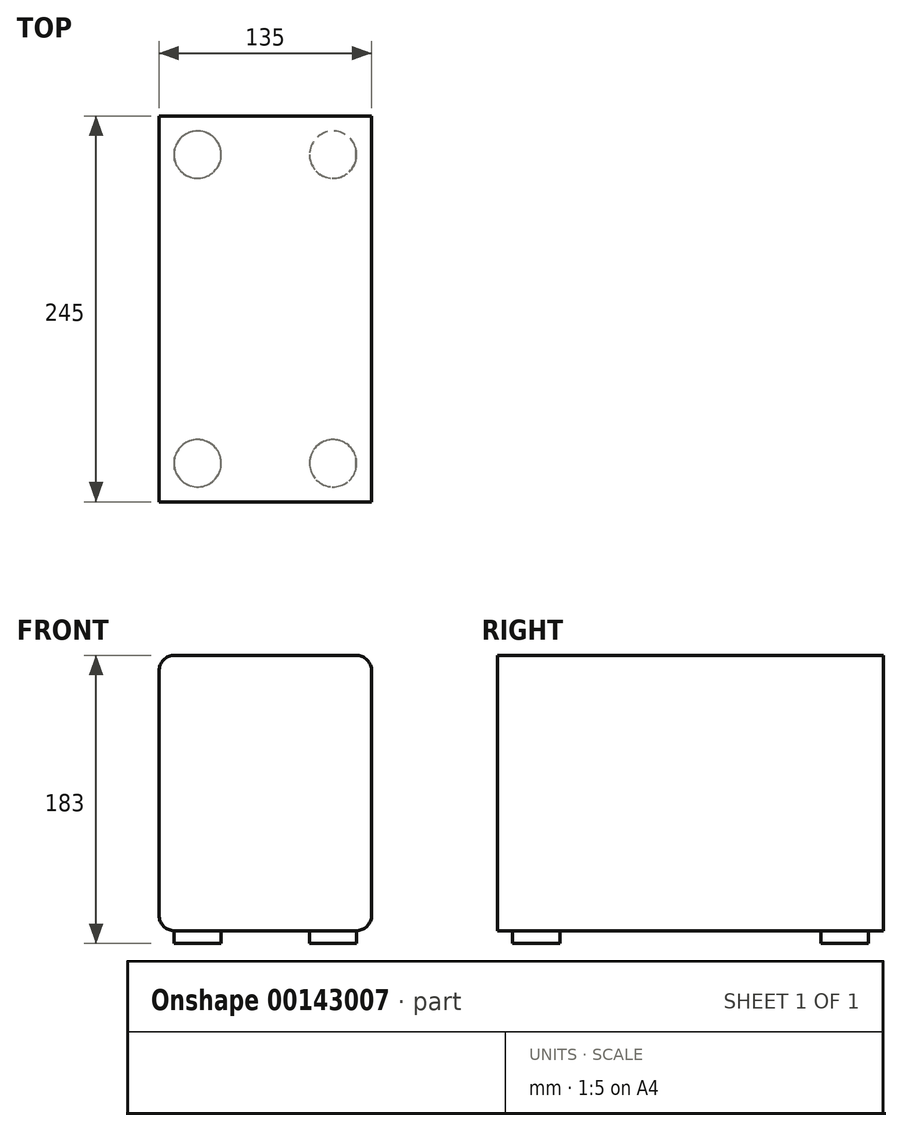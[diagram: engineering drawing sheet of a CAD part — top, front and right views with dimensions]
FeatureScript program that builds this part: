
annotation { "Feature Type Name" : "Feature", "Feature Type Description" : "" }
export const myFeature = defineFeature(function(context is Context, id is Id, definition is map)
    precondition{}
    {
        {
            var Q0;
            Q0=qCreatedBy(makeId("Front.planeOp"),FACE);
            var sketch = newSketch(context, id + "F0", { "sketchPlane" : qUnion([Q0])});
            skLineSegment(sketch, "E0.bottom", {"start": v(10, 0) * mm, "end": v(125, 0) * mm});
            skLineSegment(sketch, "E0.top", {"start": v(10, 175) * mm, "end": v(125, 175) * mm});
            skLineSegment(sketch, "E0.left", {"start": v(0, 10) * mm, "end": v(0, 165) * mm});
            skLineSegment(sketch, "E0.right", {"start": v(135, 10) * mm, "end": v(135, 165) * mm});
            skPoint(sketch, "E1.visualSharp", {"position": v(135, 175) * mm});
            skArc(sketch, "E1.filletArc", {"start": v(135, 165) * mm, "mid": v(132.07, 172.07) * mm, "end": v(125, 175) * mm});
            skPoint(sketch, "E2.visualSharp", {"position": v(0, 175) * mm});
            skArc(sketch, "E2.filletArc", {"start": v(10, 175) * mm, "mid": v(2.93, 172.07) * mm, "end": v(0, 165) * mm});
            skPoint(sketch, "E3.visualSharp", {"position": v(135, 0) * mm});
            skArc(sketch, "E3.filletArc", {"start": v(125, 0) * mm, "mid": v(132.07, 2.93) * mm, "end": v(135, 10) * mm});
            skPoint(sketch, "E4.visualSharp", {"position": v(0, 0) * mm});
            skArc(sketch, "E4.filletArc", {"start": v(0, 10) * mm, "mid": v(2.93, 2.93) * mm, "end": v(10, 0) * mm});
            skSolve(sketch);
        }
        {
            var Q0;
            Q0 = qSketchRegion(id + "F0", true);
            extrude(context, id + "F1", {"entities" : qUnion([Q0]), "depth" : 245 * mm});
        }
        {
            var Q0;
            Q0=makeQuery(id+"F1.opExtrude","SWEPT_FACE",FACE,{"disambiguationData":[OSD([sQuery(id+"F0.wireOp",EDGE,"E0.bottom")])]});
            var sketch = newSketch(context, id + "F2", { "sketchPlane" : qUnion([Q0])});
            skPoint(sketch, "E5", {"position": v(24.48, 220.52) * mm});
            skCircle(sketch, "E6", {"center": v(24.48, 220.52) * mm, "radius": 15 * mm});
            skLineSegment(sketch, "E7", {"start": v(67.5, 253.64) * mm, "end": v(67.5, 0) * mm, "construction": true});
            skPoint(sketch, "E7.startSnap0", {"position": v(67.5, 245) * mm});
            skCircle(sketch, "E8.MirrorC", {"center": v(110.52, 220.52) * mm, "radius": 15 * mm});
            skLineSegment(sketch, "E9", {"start": v(10, 122.5) * mm, "end": v(125, 122.5) * mm, "construction": true});
            skCircle(sketch, "E10.MirrorC", {"center": v(24.48, 24.48) * mm, "radius": 15 * mm});
            skCircle(sketch, "E11.MirrorC", {"center": v(110.52, 24.48) * mm, "radius": 15 * mm});
            skPoint(sketch, "E12.MirrorP", {"position": v(67.5, 0) * mm});
            skLineSegment(sketch, "E13.MirrorCS", {"start": v(67.5, -8.64) * mm, "end": v(67.5, 245) * mm, "construction": true});
            skSolve(sketch);
        }
        {
            var Q0;
            Q0 = qSketchRegion(id + "F2", true);
            extrude(context, id + "F3", {"entities" : qUnion([Q0]), "operationType" : NewBodyOperationType.ADD, "depth" : 8 * mm});
        }
    });
